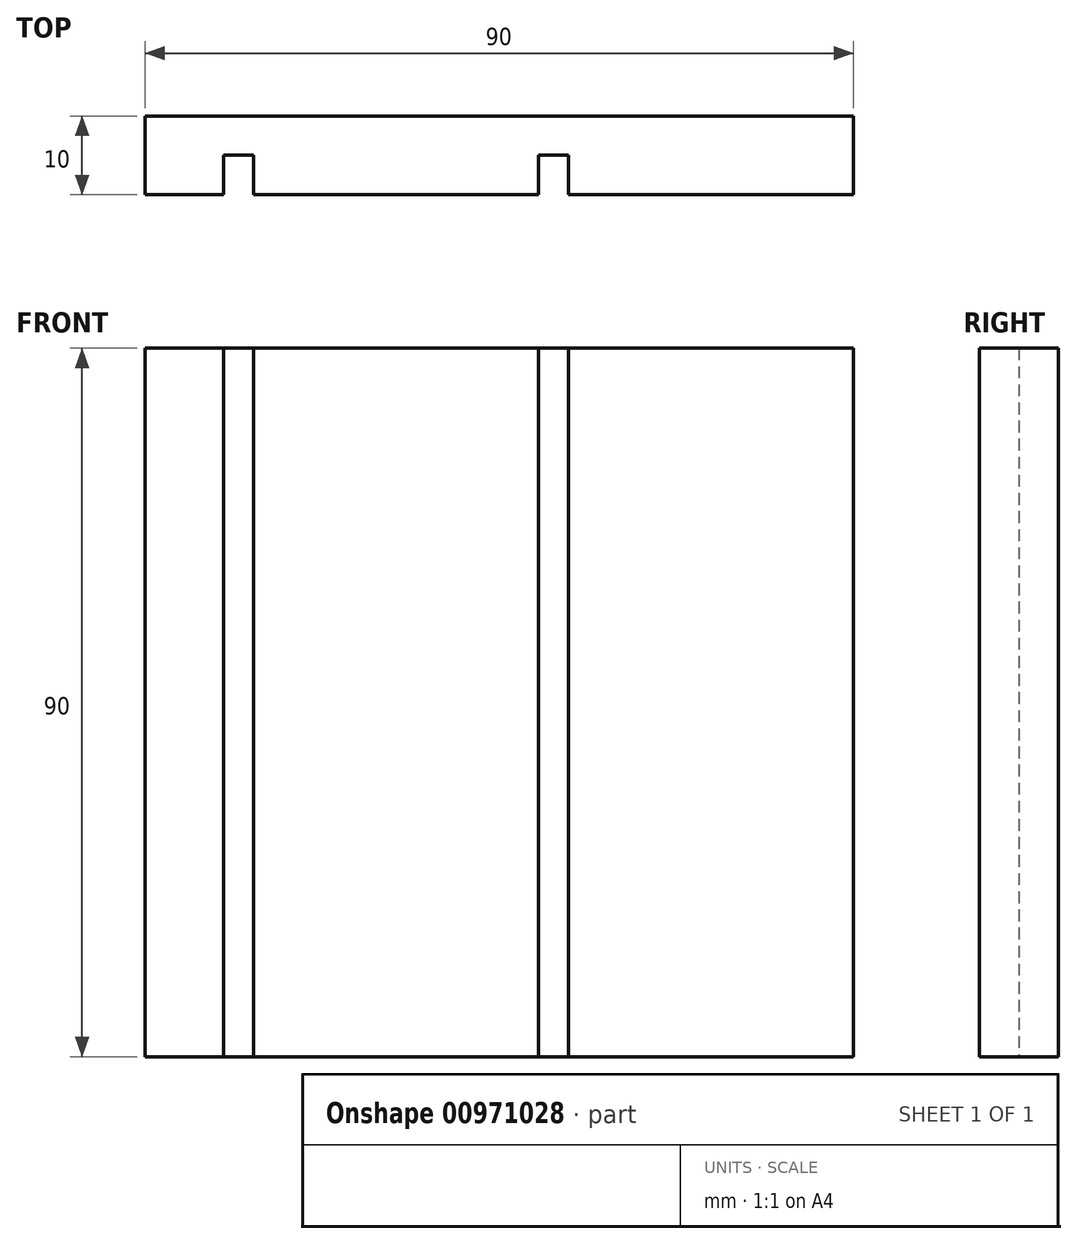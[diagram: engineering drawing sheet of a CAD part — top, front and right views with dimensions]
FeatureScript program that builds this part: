
annotation { "Feature Type Name" : "Feature", "Feature Type Description" : "" }
export const myFeature = defineFeature(function(context is Context, id is Id, definition is map)
    precondition{}
    {
        {
            var Q0;
            Q0=qCreatedBy(makeId("Front.planeOp"),FACE);
            var sketch = newSketch(context, id + "F0", { "sketchPlane" : qUnion([Q0])});
            skLineSegment(sketch, "E0.bottom", {"start": v(45, -45) * mm, "end": v(-45, -45) * mm});
            skLineSegment(sketch, "E0.top", {"start": v(45, 45) * mm, "end": v(-45, 45) * mm});
            skLineSegment(sketch, "E0.left", {"start": v(45, -45) * mm, "end": v(45, 45) * mm});
            skLineSegment(sketch, "E0.right", {"start": v(-45, -45) * mm, "end": v(-45, 45) * mm});
            skPoint(sketch, "E0.middle", {"position": v(0, 0) * mm});
            skSolve(sketch);
        }
        {
            var Q0;
            Q0 = qSketchRegion(id + "F0", true);
            extrude(context, id + "F1", {"entities" : qUnion([Q0]), "oppositeDirection" : true, "depth" : 10 * mm, "offsetDistance" : 25 * mm});
        }
        {
            var Q0;
            Q0=makeQuery(id+"F1.opExtrude","SWEPT_FACE",FACE,{"disambiguationData":[OSD([sQuery(id+"F0.wireOp",EDGE,"E0.bottom")])]});
            var sketch = newSketch(context, id + "F2", { "sketchPlane" : qUnion([Q0])});
            skLineSegment(sketch, "E1", {"start": v(-35, 0) * mm, "end": v(-35, -5) * mm});
            skLineSegment(sketch, "E2", {"start": v(-35, -5) * mm, "end": v(-31.2, -5) * mm});
            skLineSegment(sketch, "E3", {"start": v(-31.2, -5) * mm, "end": v(-31.2, 0) * mm});
            skLineSegment(sketch, "E4", {"start": v(-31.2, 0) * mm, "end": v(-35, 0) * mm});
            skLineSegment(sketch, "E5.1.0.0", {"start": v(5, 0) * mm, "end": v(5, -5) * mm});
            skLineSegment(sketch, "E5.1.0.1", {"start": v(8.8, 0) * mm, "end": v(5, 0) * mm});
            skLineSegment(sketch, "E5.1.0.2", {"start": v(8.8, -5) * mm, "end": v(8.8, 0) * mm});
            skLineSegment(sketch, "E5.1.0.3", {"start": v(5, -5) * mm, "end": v(8.8, -5) * mm});
            skLineSegment(sketch, "E5.direction1", {"start": v(-35, -5) * mm, "end": v(5, -5) * mm, "construction": true});
            skSolve(sketch);
        }
        {
            var Q0;
            Q0 = qSketchRegion(id + "F2", true);
            extrude(context, id + "F3", {"entities" : qUnion([Q0]), "operationType" : NewBodyOperationType.REMOVE, "endBound" : BoundingType.THROUGH_ALL, "oppositeDirection" : true, "depth" : 25 * mm, "offsetDistance" : 25 * mm});
        }
    });
